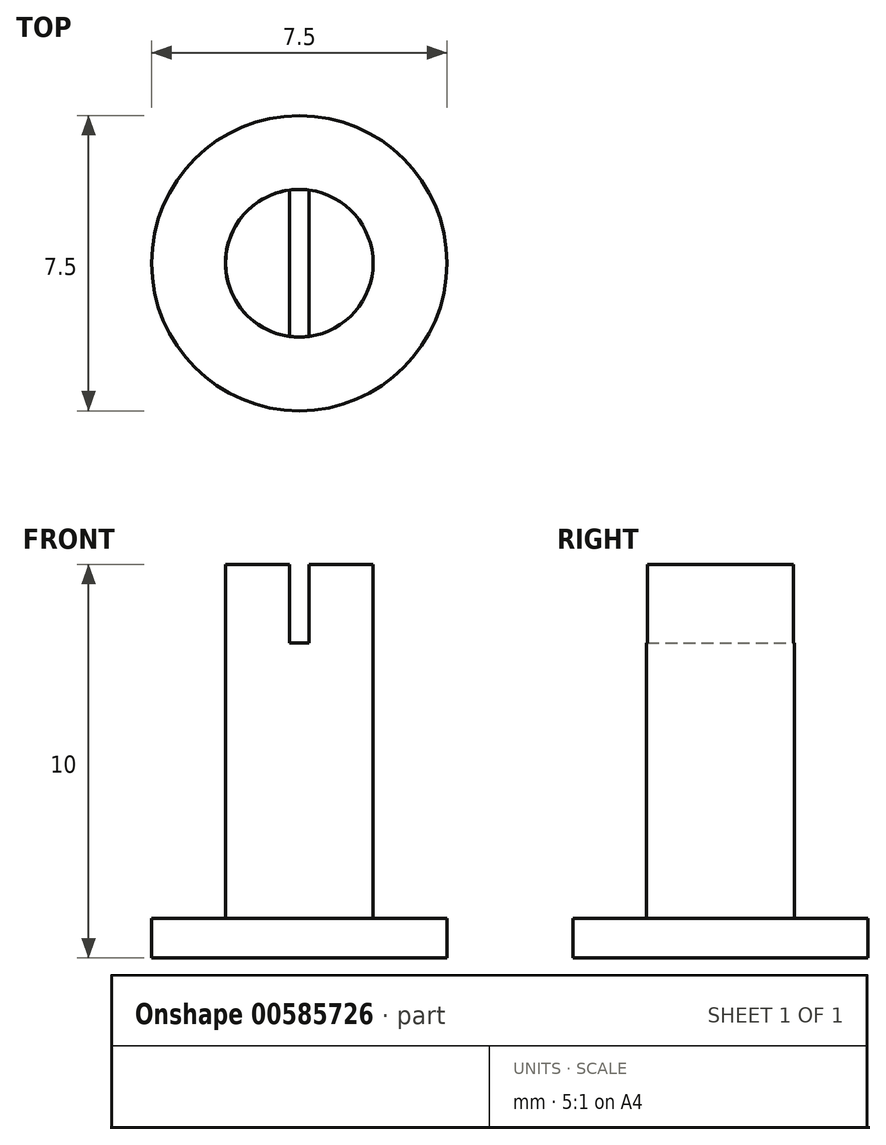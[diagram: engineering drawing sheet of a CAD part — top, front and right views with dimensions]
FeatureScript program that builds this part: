
annotation { "Feature Type Name" : "Feature", "Feature Type Description" : "" }
export const myFeature = defineFeature(function(context is Context, id is Id, definition is map)
    precondition{}
    {
        {
            var Q0;
            Q0=qCreatedBy(makeId("Top.planeOp"),FACE);
            var sketch = newSketch(context, id + "F0", { "sketchPlane" : qUnion([Q0])});
            skCircle(sketch, "E0", {"center": v(0, 0) * mm, "radius": 3.75 * mm});
            skCircle(sketch, "E1", {"center": v(0, 0) * mm, "radius": 1.88 * mm});
            skSolve(sketch);
        }
        {
            var Q0;
            Q0=makeQuery(id+"F0.imprint","IMPRINT",FACE,{"disambiguationData":[TD([[makeQuery(id+"F0.imprint","IMPRINT",EDGE,{"derivedFrom":sQuery(id+"F0.wireOp",EDGE,"E1")}),1.0]])]});
            extrude(context, id + "F1", {"entities" : qUnion([Q0]), "depth" : 10 * mm, "offsetDistance" : 25 * mm});
        }
        {
            var Q0;
            Q0=qSketchRegion(id+"F0",true);
            extrude(context, id + "F2", {"entities" : qUnion([Q0]), "operationType" : NewBodyOperationType.ADD, "depth" : 1 * mm, "offsetDistance" : 25 * mm});
        }
        {
            var Q0;
            Q0=makeQuery(id+"F1.opExtrude","CAP_FACE",FACE,{"disambiguationData":[OSD([sQuery(id+"F0.wireOp",EDGE,"E1")])],"isStart":false});
            var sketch = newSketch(context, id + "F3", { "sketchPlane" : qUnion([Q0])});
            skLineSegment(sketch, "E2.bottom", {"start": v(-0.25, -2.5) * mm, "end": v(0.25, -2.5) * mm});
            skLineSegment(sketch, "E2.top", {"start": v(-0.25, 2.5) * mm, "end": v(0.25, 2.5) * mm});
            skLineSegment(sketch, "E2.left", {"start": v(-0.25, -2.5) * mm, "end": v(-0.25, 2.5) * mm});
            skLineSegment(sketch, "E2.right", {"start": v(0.25, -2.5) * mm, "end": v(0.25, 2.5) * mm});
            skPoint(sketch, "E2.middle", {"position": v(0, 0) * mm});
            skSolve(sketch);
        }
        {
            var Q0;
            {var subQ0=sQuery(id+"F3.wireOp",EDGE,"E2.left");var subQ1=makeQuery(id+"F1.opExtrude","CAP_EDGE",EDGE,{"disambiguationData":[OSD([sQuery(id+"F0.wireOp",EDGE,"E1")])],"isStart":false});var subQ2=makeQuery(id+"F3.imprint","INTERSECT",VERTEX,{"disambiguationData":[OD(0.0)],"derivedFrom":[subQ1,subQ0]});Q0=makeQuery(id+"F3.imprint","IMPRINT",FACE,{"disambiguationData":[TD([[makeQuery(id+"F3.imprint","IMPRINT",EDGE,{"disambiguationData":[TD([[subQ2,-1.0]])],"derivedFrom":subQ0}),-1.0]])]});}
            extrude(context, id + "F4", {"entities" : qUnion([Q0]), "operationType" : NewBodyOperationType.REMOVE, "oppositeDirection" : true, "depth" : 2 * mm, "offsetDistance" : 25 * mm});
        }
    });
